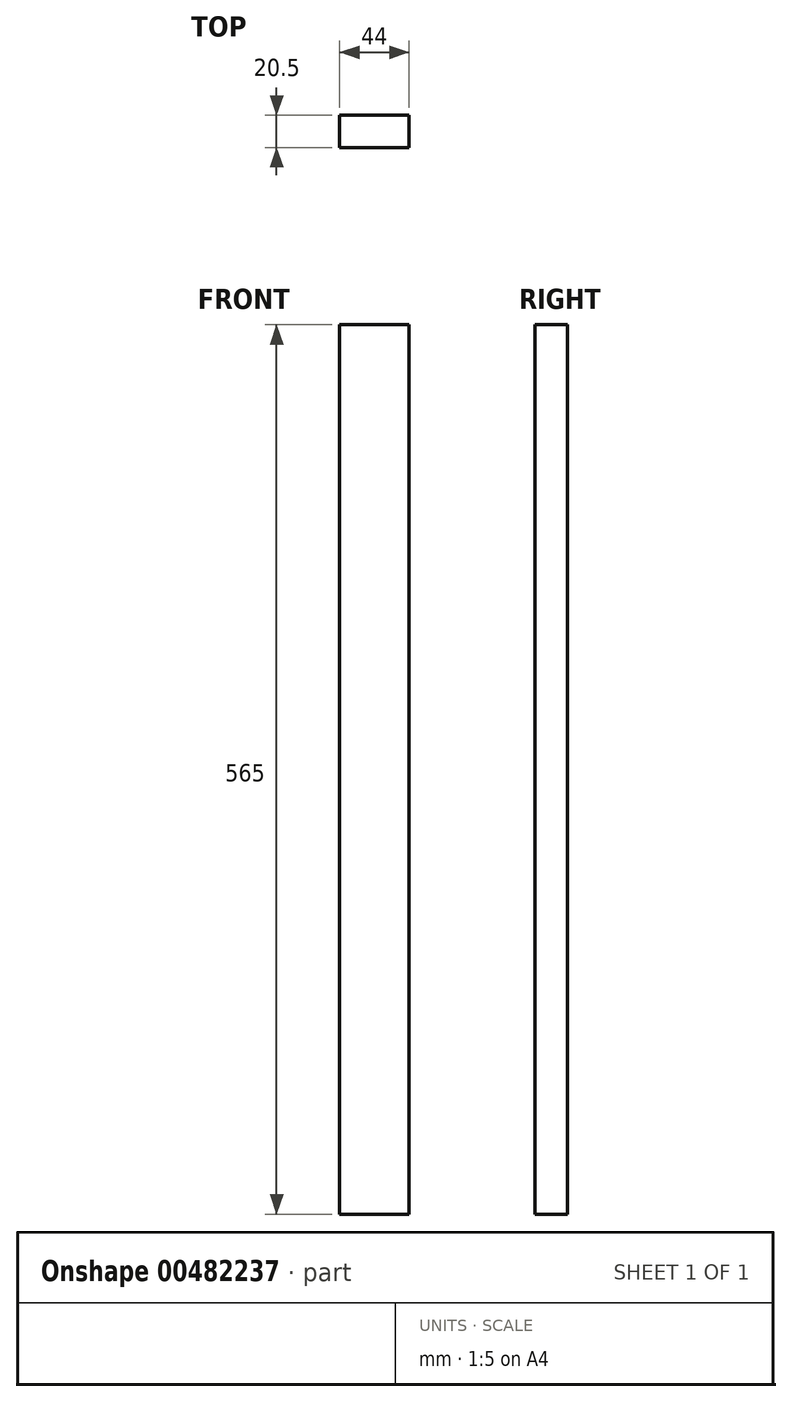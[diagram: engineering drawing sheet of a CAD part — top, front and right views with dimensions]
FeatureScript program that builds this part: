
annotation { "Feature Type Name" : "Feature", "Feature Type Description" : "" }
export const myFeature = defineFeature(function(context is Context, id is Id, definition is map)
    precondition{}
    {
        {
            var Q0;
            Q0=qCreatedBy(makeId("Top.planeOp"),FACE);
            var sketch = newSketch(context, id + "F0", { "sketchPlane" : qUnion([Q0])});
            skLineSegment(sketch, "E0.bottom", {"start": v(-22, 10.25) * mm, "end": v(22, 10.25) * mm});
            skLineSegment(sketch, "E0.top", {"start": v(-22, -10.25) * mm, "end": v(22, -10.25) * mm});
            skLineSegment(sketch, "E0.left", {"start": v(-22, 10.25) * mm, "end": v(-22, -10.25) * mm});
            skLineSegment(sketch, "E0.right", {"start": v(22, 10.25) * mm, "end": v(22, -10.25) * mm});
            skPoint(sketch, "E0.middle", {"position": v(0, 0) * mm});
            skSolve(sketch);
        }
        {
            var Q0;
            Q0 = qSketchRegion(id + "F0", true);
            extrude(context, id + "F1", {"entities" : qUnion([Q0]), "depth" : 565 * mm});
        }
    });
